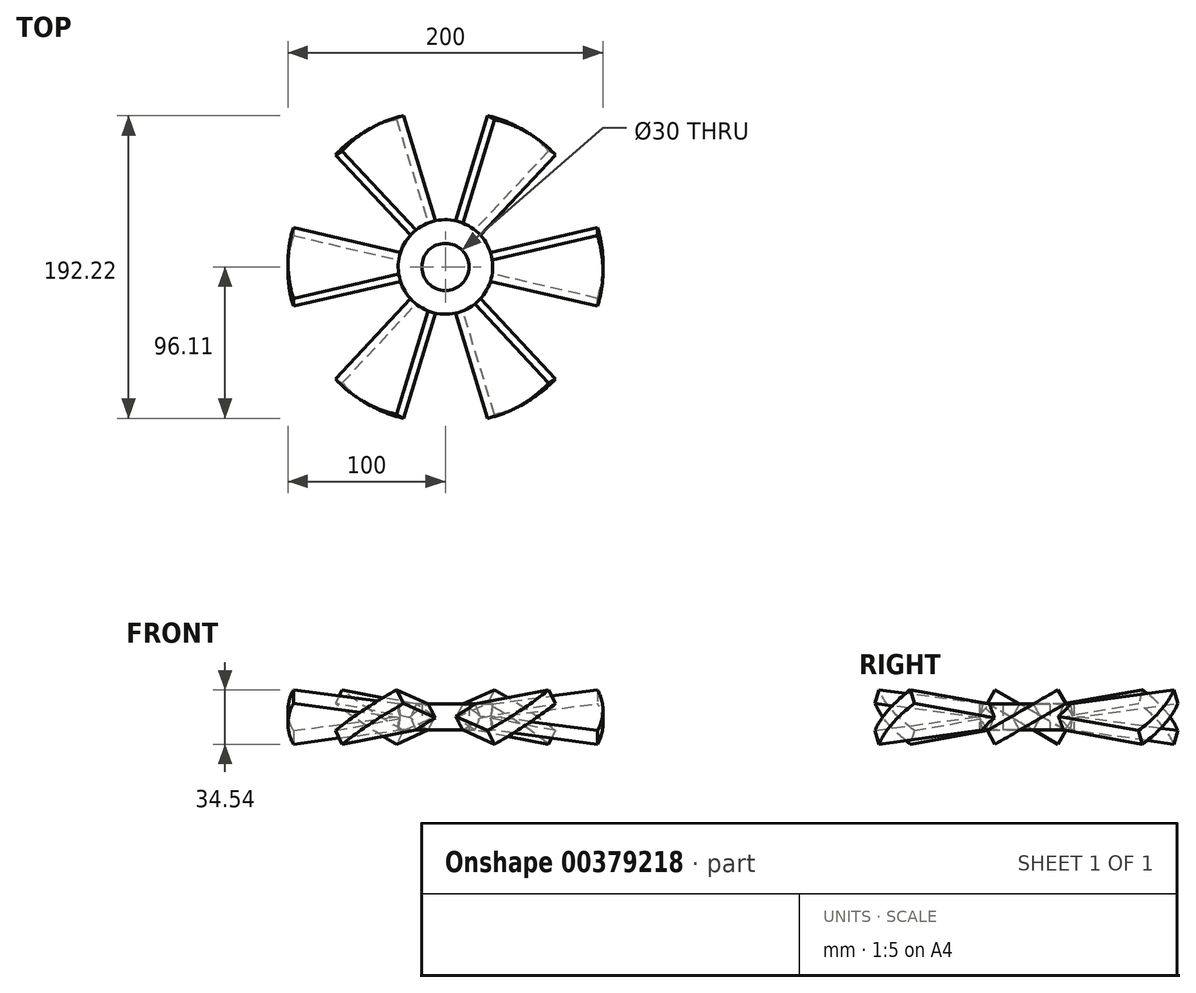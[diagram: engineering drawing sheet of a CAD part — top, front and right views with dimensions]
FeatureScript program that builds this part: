
annotation { "Feature Type Name" : "Feature", "Feature Type Description" : "" }
export const myFeature = defineFeature(function(context is Context, id is Id, definition is map)
    precondition{}
    {
        {
            var Q0;
            Q0=qCreatedBy(makeId("Top.planeOp"),FACE);
            var sketch = newSketch(context, id + "F0", { "sketchPlane" : qUnion([Q0])});
            skLineSegment(sketch, "E0", {"start": v(0, 0) * mm, "end": v(96.6, 25.88) * mm});
            skLineSegment(sketch, "E1", {"start": v(96.6, -25.88) * mm, "end": v(0, 0) * mm});
            skArc(sketch, "E2", {"start": v(96.6, 25.88) * mm, "mid": v(100, 0) * mm, "end": v(96.6, -25.88) * mm});
            skSolve(sketch);
        }
        {
            var Q0;
            Q0=makeQuery(id+"F0.imprint","IMPRINT",FACE,{"disambiguationData":[TD([[makeQuery(id+"F0.imprint","IMPRINT",EDGE,{"derivedFrom":sQuery(id+"F0.wireOp",EDGE,"E0")}),-1.0]])]});
            extrude(context, id + "F1", {"entities" : qUnion([Q0]), "depth" : 5 * mm, "hasSecondDirection" : true, "secondDirectionOppositeDirection" : true, "secondDirectionDepth" : 5 * mm});
        }
        {
            var Q0;
            Q0=qCreatedBy(makeId("Top.planeOp"),FACE);
            var sketch = newSketch(context, id + "F2", { "sketchPlane" : qUnion([Q0])});
            skLineSegment(sketch, "E3", {"start": v(0, 0) * mm, "end": v(108.83, 0) * mm, "construction": true});
            skSolve(sketch);
        }
        {
            var Q0;
            Q0=makeQuery(id+"F1.opExtrude","SWEPT_BODY",BODY,{"disambiguationData":[OSD([sQuery(id+"F0.wireOp",EDGE,"E0"),sQuery(id+"F0.wireOp",EDGE,"E1"),sQuery(id+"F0.wireOp",EDGE,"E2")])]});
            var Q1;
            Q1=sQuery(id+"F2.wireOp",EDGE,"E3");
            transform(context, id + "F3", {"entities" : qUnion([Q0]), "transformType" : TransformType.ROTATION, "transformAxis" : qUnion([Q1]), "angle" : 30 * degree, "makeCopy" : false});
        }
        {
            var Q0;
            Q0=qCreatedBy(makeId("Front.planeOp"),FACE);
            var sketch = newSketch(context, id + "F4", { "sketchPlane" : qUnion([Q0])});
            skLineSegment(sketch, "E4", {"start": v(0, 96.71) * mm, "end": v(0, 0) * mm, "construction": true});
            skSolve(sketch);
        }
        {
            var Q0;
            Q0=makeQuery(id+"F1.opExtrude","SWEPT_BODY",BODY,{"disambiguationData":[OSD([sQuery(id+"F0.wireOp",EDGE,"E0"),sQuery(id+"F0.wireOp",EDGE,"E1"),sQuery(id+"F0.wireOp",EDGE,"E2")])]});
            var Q1;
            Q1=sQuery(id+"F4.wireOp",EDGE,"E4");
            circularPattern(context, id + "F5", {"entities" : qUnion([Q0]), "axis" : qUnion([Q1]), "angle" : 360 * degree, "instanceCount" : 6, "equalSpace" : true});
        }
        {
            var Q0;
            Q0=qCreatedBy(makeId("Top.planeOp"),FACE);
            var sketch = newSketch(context, id + "F6", { "sketchPlane" : qUnion([Q0])});
            skCircle(sketch, "E5", {"center": v(0, 0) * mm, "radius": 30 * mm});
            skSolve(sketch);
        }
        {
            var Q0;
            Q0=makeQuery(id+"F6.imprint","IMPRINT",FACE,{"disambiguationData":[TD([[makeQuery(id+"F6.imprint","IMPRINT",EDGE,{"derivedFrom":sQuery(id+"F6.wireOp",EDGE,"E5")}),1.0]])]});
            extrude(context, id + "F7", {"entities" : qUnion([Q0]), "depth" : 25 * mm, "hasSecondDirection" : true, "secondDirectionOppositeDirection" : true, "secondDirectionDepth" : 25 * mm});
        }
        {
            var Q0;
            Q0=makeQuery(id+"F5.opPattern","COPY",BODY,{"derivedFrom":makeQuery(id+"F1.opExtrude","SWEPT_BODY",BODY,{"disambiguationData":[OSD([sQuery(id+"F0.wireOp",EDGE,"E0"),sQuery(id+"F0.wireOp",EDGE,"E1"),sQuery(id+"F0.wireOp",EDGE,"E2")])]}),"instanceName":"5"});
            var Q1;
            Q1=makeQuery(id+"F1.opExtrude","SWEPT_BODY",BODY,{"disambiguationData":[OSD([sQuery(id+"F0.wireOp",EDGE,"E0"),sQuery(id+"F0.wireOp",EDGE,"E1"),sQuery(id+"F0.wireOp",EDGE,"E2")])]});
            var Q2;
            Q2=makeQuery(id+"F5.opPattern","COPY",BODY,{"derivedFrom":makeQuery(id+"F1.opExtrude","SWEPT_BODY",BODY,{"disambiguationData":[OSD([sQuery(id+"F0.wireOp",EDGE,"E0"),sQuery(id+"F0.wireOp",EDGE,"E1"),sQuery(id+"F0.wireOp",EDGE,"E2")])]}),"instanceName":"2"});
            var Q3;
            Q3=makeQuery(id+"F5.opPattern","COPY",BODY,{"derivedFrom":makeQuery(id+"F1.opExtrude","SWEPT_BODY",BODY,{"disambiguationData":[OSD([sQuery(id+"F0.wireOp",EDGE,"E0"),sQuery(id+"F0.wireOp",EDGE,"E1"),sQuery(id+"F0.wireOp",EDGE,"E2")])]}),"instanceName":"1"});
            var Q4;
            Q4=makeQuery(id+"F5.opPattern","COPY",BODY,{"derivedFrom":makeQuery(id+"F1.opExtrude","SWEPT_BODY",BODY,{"disambiguationData":[OSD([sQuery(id+"F0.wireOp",EDGE,"E0"),sQuery(id+"F0.wireOp",EDGE,"E1"),sQuery(id+"F0.wireOp",EDGE,"E2")])]}),"instanceName":"3"});
            var Q5;
            Q5=makeQuery(id+"F5.opPattern","COPY",BODY,{"derivedFrom":makeQuery(id+"F1.opExtrude","SWEPT_BODY",BODY,{"disambiguationData":[OSD([sQuery(id+"F0.wireOp",EDGE,"E0"),sQuery(id+"F0.wireOp",EDGE,"E1"),sQuery(id+"F0.wireOp",EDGE,"E2")])]}),"instanceName":"4"});
            var Q6;
            Q6=makeQuery(id+"F7.opExtrude","SWEPT_BODY",BODY,{"disambiguationData":[OSD([sQuery(id+"F6.wireOp",EDGE,"E5")])]});
            booleanBodies(context, id + "F8", {"operationType" : BooleanOperationType.UNION, "tools" : qUnion([Q0, Q1, Q2, Q3, Q4, Q5, Q6])});
        }
        {
            var Q0;
            {var subQ0=sQuery(id+"F0.wireOp",EDGE,"E0");Q0=makeQuery(id+"F8.opBoolean","INTERSECT",VERTEX,{"derivedFrom":[makeQuery(id+"F5.opPattern","COPY",FACE,{"derivedFrom":makeQuery(id+"F1.opExtrude","SWEPT_FACE",FACE,{"disambiguationData":[OSD([subQ0])]}),"instanceName":"2"}),makeQuery(id+"F5.opPattern","COPY",FACE,{"derivedFrom":makeQuery(id+"F1.opExtrude","CAP_FACE",FACE,{"disambiguationData":[OSD([subQ0,sQuery(id+"F0.wireOp",EDGE,"E1"),sQuery(id+"F0.wireOp",EDGE,"E2")])],"isStart":false}),"instanceName":"2"}),makeQuery(id+"F7.opExtrude","SWEPT_FACE",FACE,{"disambiguationData":[OSD([sQuery(id+"F6.wireOp",EDGE,"E5")])]})]});}
            var Q1;
            {var subQ0=sQuery(id+"F0.wireOp",EDGE,"E0");Q1=makeQuery(id+"F8.opBoolean","INTERSECT",VERTEX,{"derivedFrom":[makeQuery(id+"F5.opPattern","COPY",FACE,{"derivedFrom":makeQuery(id+"F1.opExtrude","SWEPT_FACE",FACE,{"disambiguationData":[OSD([subQ0])]}),"instanceName":"1"}),makeQuery(id+"F5.opPattern","COPY",FACE,{"derivedFrom":makeQuery(id+"F1.opExtrude","CAP_FACE",FACE,{"disambiguationData":[OSD([subQ0,sQuery(id+"F0.wireOp",EDGE,"E1"),sQuery(id+"F0.wireOp",EDGE,"E2")])],"isStart":false}),"instanceName":"1"}),makeQuery(id+"F7.opExtrude","SWEPT_FACE",FACE,{"disambiguationData":[OSD([sQuery(id+"F6.wireOp",EDGE,"E5")])]})]});}
            var Q2;
            {var subQ0=sQuery(id+"F0.wireOp",EDGE,"E0");Q2=makeQuery(id+"F8.opBoolean","INTERSECT",VERTEX,{"derivedFrom":[makeQuery(id+"F1.opExtrude","SWEPT_FACE",FACE,{"disambiguationData":[OSD([subQ0])]}),makeQuery(id+"F1.opExtrude","CAP_FACE",FACE,{"disambiguationData":[OSD([subQ0,sQuery(id+"F0.wireOp",EDGE,"E1"),sQuery(id+"F0.wireOp",EDGE,"E2")])],"isStart":false}),makeQuery(id+"F7.opExtrude","SWEPT_FACE",FACE,{"disambiguationData":[OSD([sQuery(id+"F6.wireOp",EDGE,"E5")])]})]});}
            cPlane(context, id + "F9", {"entities" : qUnion([Q0, Q1, Q2]), "cplaneType" : CPlaneType.THREE_POINT, "offset" : 25 * mm, "width" : 150 * mm, "height" : 150 * mm});
        }
        {
            var Q0;
            Q0=makeQuery(id+"F7.opExtrude","CAP_FACE",FACE,{"disambiguationData":[OSD([sQuery(id+"F6.wireOp",EDGE,"E5")])],"isStart":false});
            var Q1;
            Q1=qCreatedBy(id+"F9.planeOp",FACE);
            extrude(context, id + "F10", {"entities" : qUnion([Q0]), "operationType" : NewBodyOperationType.REMOVE, "endBound" : BoundingType.UP_TO_SURFACE, "oppositeDirection" : true, "endBoundEntityFace" : qUnion([Q1]), "depth" : 25 * mm});
        }
        {
            var Q0;
            {var subQ0=sQuery(id+"F0.wireOp",EDGE,"E1");Q0=makeQuery(id+"F8.opBoolean","INTERSECT",VERTEX,{"derivedFrom":[makeQuery(id+"F5.opPattern","COPY",FACE,{"derivedFrom":makeQuery(id+"F1.opExtrude","CAP_FACE",FACE,{"disambiguationData":[OSD([sQuery(id+"F0.wireOp",EDGE,"E0"),subQ0,sQuery(id+"F0.wireOp",EDGE,"E2")])],"isStart":true}),"instanceName":"3"}),makeQuery(id+"F5.opPattern","COPY",FACE,{"derivedFrom":makeQuery(id+"F1.opExtrude","SWEPT_FACE",FACE,{"disambiguationData":[OSD([subQ0])]}),"instanceName":"3"}),makeQuery(id+"F7.opExtrude","SWEPT_FACE",FACE,{"disambiguationData":[OSD([sQuery(id+"F6.wireOp",EDGE,"E5")])]})]});}
            var Q1;
            {var subQ0=sQuery(id+"F0.wireOp",EDGE,"E1");Q1=makeQuery(id+"F8.opBoolean","INTERSECT",VERTEX,{"derivedFrom":[makeQuery(id+"F5.opPattern","COPY",FACE,{"derivedFrom":makeQuery(id+"F1.opExtrude","CAP_FACE",FACE,{"disambiguationData":[OSD([sQuery(id+"F0.wireOp",EDGE,"E0"),subQ0,sQuery(id+"F0.wireOp",EDGE,"E2")])],"isStart":true}),"instanceName":"4"}),makeQuery(id+"F5.opPattern","COPY",FACE,{"derivedFrom":makeQuery(id+"F1.opExtrude","SWEPT_FACE",FACE,{"disambiguationData":[OSD([subQ0])]}),"instanceName":"4"}),makeQuery(id+"F7.opExtrude","SWEPT_FACE",FACE,{"disambiguationData":[OSD([sQuery(id+"F6.wireOp",EDGE,"E5")])]})]});}
            var Q2;
            {var subQ0=sQuery(id+"F0.wireOp",EDGE,"E1");Q2=makeQuery(id+"F8.opBoolean","INTERSECT",VERTEX,{"derivedFrom":[makeQuery(id+"F5.opPattern","COPY",FACE,{"derivedFrom":makeQuery(id+"F1.opExtrude","CAP_FACE",FACE,{"disambiguationData":[OSD([sQuery(id+"F0.wireOp",EDGE,"E0"),subQ0,sQuery(id+"F0.wireOp",EDGE,"E2")])],"isStart":true}),"instanceName":"1"}),makeQuery(id+"F5.opPattern","COPY",FACE,{"derivedFrom":makeQuery(id+"F1.opExtrude","SWEPT_FACE",FACE,{"disambiguationData":[OSD([subQ0])]}),"instanceName":"1"}),makeQuery(id+"F7.opExtrude","SWEPT_FACE",FACE,{"disambiguationData":[OSD([sQuery(id+"F6.wireOp",EDGE,"E5")])]})]});}
            cPlane(context, id + "F11", {"entities" : qUnion([Q0, Q1, Q2]), "cplaneType" : CPlaneType.THREE_POINT, "offset" : 25 * mm, "width" : 150 * mm, "height" : 150 * mm});
        }
        {
            var Q0;
            Q0=makeQuery(id+"F7.opExtrude","CAP_FACE",FACE,{"disambiguationData":[OSD([sQuery(id+"F6.wireOp",EDGE,"E5")])],"isStart":true});
            var Q1;
            Q1=qCreatedBy(id+"F11.planeOp",FACE);
            extrude(context, id + "F12", {"entities" : qUnion([Q0]), "operationType" : NewBodyOperationType.REMOVE, "endBound" : BoundingType.UP_TO_SURFACE, "oppositeDirection" : true, "endBoundEntityFace" : qUnion([Q1]), "depth" : 25 * mm});
        }
        {
            var Q0;
            Q0=qCreatedBy(id+"F11.planeOp",FACE);
            var sketch = newSketch(context, id + "F13", { "sketchPlane" : qUnion([Q0])});
            skCircle(sketch, "E6", {"center": v(0, 0) * mm, "radius": 15 * mm});
            skSolve(sketch);
        }
        {
            var Q0;
            Q0 = qSketchRegion(id + "F13", true);
            extrude(context, id + "F14", {"entities" : qUnion([Q0]), "operationType" : NewBodyOperationType.REMOVE, "depth" : 25 * mm});
        }
    });
